# Revit family: KBB d=500_Precast-Console Beam_Spæncom
name_source: partatom
category: Structural Framing
revit_build: Autodesk Revit 2014 (Build: 20130308_1515(x64)
units: mm (PartAtom-declared; Revit-internal decimal feet)

## types (4) — shared parameters
Base width = 660 mm
Height console = 500 mm  [stored 1.64042 ft]
Manufacturer = Spæncom
Model = KBB

## per-type parameters (varying)
| type | Height (bjælkekroppen) | Height element | Width (bjælkekroppen) | Width console |
| KBB 128/78 (150mm hylde) | 780 mm  [stored 2.55906 ft] | 1280 mm  [stored 4.19948 ft] | 485 mm  [stored 1.59121 ft] | 150 mm |
| KBB 128/78 (200mm hylde) | 780 mm  [stored 2.55906 ft] | 1280 mm  [stored 4.19948 ft] | 385 mm  [stored 1.26312 ft] | 200 mm  [stored 0.656168 ft] |
| KBB 140/90 (150mm hylde) | 900 mm  [stored 2.95276 ft] | 1400 mm  [stored 4.59318 ft] | 485 mm  [stored 1.59121 ft] | 150 mm |
| KBB 140/90 (200mm hylde) | 900 mm  [stored 2.95276 ft] | 1400 mm  [stored 4.59318 ft] | 385 mm  [stored 1.26312 ft] | 200 mm  [stored 0.656168 ft] |

note: [stored X ft] marks values corroborated as IEEE doubles in the binary element streams (Revit-internal decimal feet)

## geometry (parser evidence)
native form markers: Sweep x1
no freeform markers — native parametric forms only
